# Revit family: PD4-FP types Avec hôte
name_source: partatom
category: Dispositifs d'éclairage
units: mm (PartAtom-declared; Revit-internal decimal feet)

## family parameters
Conserver l'orientation des annotations = Oui
Cote de connecteur circulaire = Utiliser le diamètre
Couper avec des vides une fois chargée = Non
Hôte = Face
Partagée = Non
Point de calcul de pièce = Non
Type d'élément = Normal

## types (28) — shared parameters
Classe = II
Code d'assemblage = D5010200
Fabricant = B.E.G.
Hauteur de montage max = 350 cm
Image du type = 360°.jpg
Marque = LUXOMAT
Mode de pose = Faux Plafond
URL = https://www.beg-luxomat.com
zero-valued in all types: Elévation par défaut

## per-type parameters (varying)
| type | Alimentation | Charge Cos ɸ =0.5 | Charge Cos ɸ =1 | Charge LED | Commentaires du type | Consommation | IP | Modèle | Relais | Référence | Température ambiante | Type de Sortie |
| 01- PD4-FP Générique | 110-240 V AC |  |  |  | DET.PRES.360°/Ø24M FAUX PLAFOND |  | 20 | PD4-FP |  |  | -25°C à +50°C |  |
| 02- PD4N-1C-FP réf 92149 | 110-240 V AC | 1150 VA | 2300 W | 300 W | DET.MOUV.1 CONTACT.360°/Ø24M FAUX PLAFOND | 0,25 W | 23 | PD4N-1C-FP | 10 A | 92149 | -25°C à +50°C | TOR |
| 03- PD4-M-1C-FP réf 92585 | 110-240 V AC | 1150 VA | 2300 W | 300 W | DET.PRES.MAITRE.1 CONTACT.360°/Ø24M FAUX PLAFOND | 0,45 W | 20 | PD4-M-1C-FP | 10 A | 92585 | -25°C à +50°C | TOR |
| 04- PD4-M-2C-FP réf 92148 | 110-240 V AC | 1150 VA | 2300 W | 300 W | DET.PRES.MAITRE.2 CONTACTS.360°/Ø24M FAUX PLAFOND | 0,47 W | 20 | PD4-M-2C-FP | 10 A / 3 A | 92148 | -25°C à +50°C | TOR + CVC |
| 05- PD4-M-2C-DUO-FP réf 92251 | 110-240 V AC | 1150 VA | 2300 W | 300 W | DET.PRES.MAITRE.DUO.2 CONTACTS.360°/Ø24M FAUX PLAFOND | 0,47 W | 20 | PD4-M-2C-DUO-FP | 10 A | 92251 | -25°C à +50°C | 2  TOR (1er jour/2ème jour) |
| 06- PD4-M-3C-TRIO-FP réf 92745 | 110-240 V AC | 1500 VA | 3000 W | 300 W | DET.PRES.MAITRE.TRIO.3 CONTACTS.360°/Ø24M FAUX PLAFOND | 0,58 W | 20 | PD4-M-3C-TRIO-FP | 16 A | 92745 | -25°C à +50°C | 3  TOR (1er jour/2ème jour + Tableau ou CVC) |
| 13- PD4-M-DIM-FP réf 92247 | 110-240 V AC | 1150 VA | 2300 W | 300 W | DET.PRES.MAITRE.DIM(1-10V).360°/Ø24M FAUX PLAFOND | 0,50 W | 20 | PD4-M-DIM-FP | 10 A | 92247 | -25°C à +50°C | DIM (50 ballasts maxi) |
| 14- PD4-M-DIM-CVC-FP réf 92507 | 110-240 V AC | 1150 VA | 2300 W | 300 W | DET.PRES.MAITRE.DIM(1-10V) + CVC 3A.360°/Ø24M FAUX PLAFOND | 0,50 W | 20 | PD4-M-DIM-CVC-FP | 10 A / 3 A | 92507 | -25°C à +50°C | DIM (50 ballasts maxi) + CVC |
| 15- PD4-M-DIM-CVC-16A-FP réf 92547 | 110-240 V AC | 1150 VA / 1500 VA | 2300 W / 3000 W | 300 W / 300 W | DET.PRES.MAITRE.DIM(1-10V) + CVC 16A.360°/Ø24M FAUX PLAFOND | 0,54 W | 20 | PD4-M-DIM-CVC-16A-FP | 10 A / 16 A | 92547 | -25°C à +50°C | DIM (50 ballasts maxi) + CVC |
| 16- PD4-M-DUO-DIM-FP réf 92272 | 110-240 V AC | 1150 VA | 2300 W | 300 W | DET.PRES.MAITRE.DUO.2 DIM(1-10V).360°/Ø24M FAUX PLAFOND | 0,50 W | 20 | PD4-M-DUO-DIM-FP | 10 A | 92272 | -25°C à +50°C | 2 DIM (25 ballasts maxi-1er jour/2ème jour) |
| 17- PD4-M-TRIO-DIM-FP réf 92735 | 110-240 V AC | 1500 VA | 3000 W | 300 W | DET.PRES.MAITRE.TRIO.2 DIM(1-10V) + TOR.360°/Ø24M FAUX PLAFOND | 0,78 W | 20 | PD4-M-TRIO-DIM-FP | 16 A | 92735 | -25°C à +50°C | 2 DIM (25 ballasts maxi-1er jour/2ème jour) + TOR (Tableau ou CVC) |
| 07- PD4N-M-DACO-FP réf 93460 | 110-240 V AC | 0 | 0 | 0 | DET.PRES.MAITRE.DALI 2.360°/Ø24M FAUX PLAFOND | 2 W | 20 | PD4N-M-DACO-FP | 0 | 93460 | -25°C à +50°C | DALI 2  (40 drivers maxi) |
| 08- PD4N-M-DACO-1C-FP réf 93463 | 110-240 V AC | 1150 VA | 2300 W | 300 W | DET.PRES.MAITRE.DALI 2 + CONTACT NO.360°/Ø24M FAUX PLAFOND | 2 W | 20 | PD4N-M-DACO-1C-FP | 10 A | 93463 | -25°C à +50°C | DALI 2 (40 drivers maxi) + Contact NO |
| 09- PD4-M-DUO-DALI/DSI-FP réf 92276 | 110-240 V AC | 0 | 0 | 0 | DET.PRES.MAITRE.DUO.2 DALI/DSI.360°/Ø24M FAUX PLAFOND | 0,50 W | 20 | PD4-M-DUO-DALI/DSI-FP | 0 | 92276 | -25°C à +50°C | 2 DALI (25 ballasts maxi-1er jour/2ème jour) |
| 10- PD4-M-TRIO-2DALI/DSI-1C-FP réf 92756 | 110-240 V AC | 1500 VA | 3000 W | 300 W | DET.PRES.MAITRE.TRIO.2 DALI/DSI + TOR.360°/Ø24M FAUX PLAFOND | 0,78 W | 20 | PD4-M-TRIO-2DALI/DSI-1C-FP | 16 A | 92756 | -25°C à +50°C | 2 DALI (25 ballasts maxi-1er jour/2ème jour) + TOR (Tableau ou CVC) |
| 11- PD4-M-DAA4G-FP réf 92591 | 110-240 V AC | 1150 VA | 2300 W | 300 W | DET.PRES.MAITRE.DALI ADRESSABLE AUTONOME + TOR.360°/Ø24M FAUX PLAFOND | 0.4 W | 20 | PD4-M-DAA4G-FP | 10 A | 92591 | -25°C à +50°C | DALI Adressable Autonome (64 ballasts maxi) + TOR |
| 28- PD4N-LTMS-RR-FP réf 92709 | 11-48 V DC | 0 | 0 | 0 | DET.PRES.11-48V.1 CONTACT.RR.360°/Ø24M FAUX PLAFOND | > 1 W | 20 | PD4N-LTMS-RR-FP | 100 mA | 92709 | 0°C à +50°C | Reed Relais |
| 23- PD4N-KNX-ST-FP réf 93384 | 24 V DC par bus KNX | 0 | 0 | 0 | DET.PRES.KNX.VERSION STANDARD.360°/Ø24M FAUX PLAFOND | 12 mA | 20 | PD4N-KNX-ST-FP | 0 | 93384 | -5°C à +45°C | KNX - 1 sortie Eclairage TOR ou GRADATION / 3 sorties Présence |
| 24- PD4N-KNX-DX-FP réf 93386 | 24 V DC par bus KNX | 0 | 0 | 0 | DET.PRES.KNX.VERSION DELUXE.360°/Ø24M FAUX PLAFOND | 12 mA | 20 | PD4N-KNX-DX-FP | 0 | 93386 | -5°C à +45°C | KNX - 1 sortie Eclairage TOR ou GRADATION / 3 sorties Présence / Capteur de température et bruit |
| 27- PD4N-LON-FP réf 92831 | 24 V DC par bus LON | 0 | 0 | 0 | DET.PRES.LON.360°/Ø24M FAUX PLAFOND | 12 mA | 20 | PD4N-LON-FP | 0 | 92831 | -5°C à +45°C | LON |
| 22- PD4N-BMS-DALI-2-FP réf 93546 | 10-22V DC par bus DALI | 0 | 0 | 0 | MULTI.CAPTEUR.PRES.BMS.DALI 2.360°/Ø24M FAUX PLAFOND | 7 mA | 20 | PD4N-BMS-DALI-2-FP | 0 | 93546 | -25°C à +50°C | DALI 2 adressable - BMS |
| 18- PD4-S-FP réf 92254 | 110-240 V AC | 0 | 0 | 0 | DET.PRES.ESCLAVE.360°/Ø24M FAUX PLAFOND | 0,25 W | 20 | PD4-S-FP | 0 | 92254 | -25°C à +50°C | Esclave |
| 19- PD4-S-DAA4G-FP réf 92721 | 22 V DC par bus DALI | 0 | 0 | 0 | DET.PRES.ESCLAVE.DALI.360°/Ø24M FAUX PLAFOND | 7 mA | 20 | PD4-S-DAA4G-FP | 0 | 92721 | -25°C à +50°C | DALI Esclave |
| 12- PD4-M-HCL2-FP réf 93484 | 110-240 V AC | 1150 VA | 2300 W | 300 W | DET.PRES.MAITRE.DALI HCL ADRESSABLE AUTONOME + TOR.360°/Ø24M FAUX PLAFOND | 0.4 W | 20 | PD4-M-HCL2-FP | 10 A | 93484 | -25°C à +50°C | DALI HCL Adressable Autonome (64 ballasts maxi) + TOR |
| 20- PD4N-DALILINK-FP réf 93377 | 16V DC par bus DALI | 0 | 0 | 0 | MULTI.CAPTEUR.PRES.DALILINK.360°/Ø24M FAUX PLAFOND | 7 mA | 20 | PD4N-DALILINK-FP | 0 | 93377 | -25°C à +55°C | DALILINK |
| 21- PD4N-DALISYS-FP réf 93340 | 10-22V DC par bus DALI | 0 | 0 | 0 | MULTI.CAPTEUR.PRES.DALISYS.360°/Ø24M FAUX PLAFOND | 7 mA | 20 | PD4N-DALISYS-FP | 0 | 93340 | -25°C à +55°C | DALI adressable |
| 25- PD4N-KNXs-ST-FP réf 93514 | 24 V DC par bus KNX | 0 | 0 | 0 | DET.PRES.KNX Sécure.VERSION STANDARD.360°/Ø24M FAUX PLAFOND | 12 mA | 20 | PD4N-KNXs-ST-FP | 0 | 93514 | -5°C à +45°C | KNX Sécure - 1 sortie Eclairage TOR ou GRADATION / 3 sorties Présence / HCL |
| 26- PD4N-KNXs-DX-FP réf 93516 | 24 V DC par bus KNX | 0 | 0 | 0 | DET.PRES.KNX Sécure.VERSION DELUXE.360°/Ø24M FAUX PLAFOND | 12 mA | 20 | PD4N-KNXs-DX-FP | 0 | 93516 | -5°C à +45°C | KNX Sécure - 1 sortie Eclairage TOR ou GRADATION / 3 sorties Présence / Capteur de température et bruit / HC |
